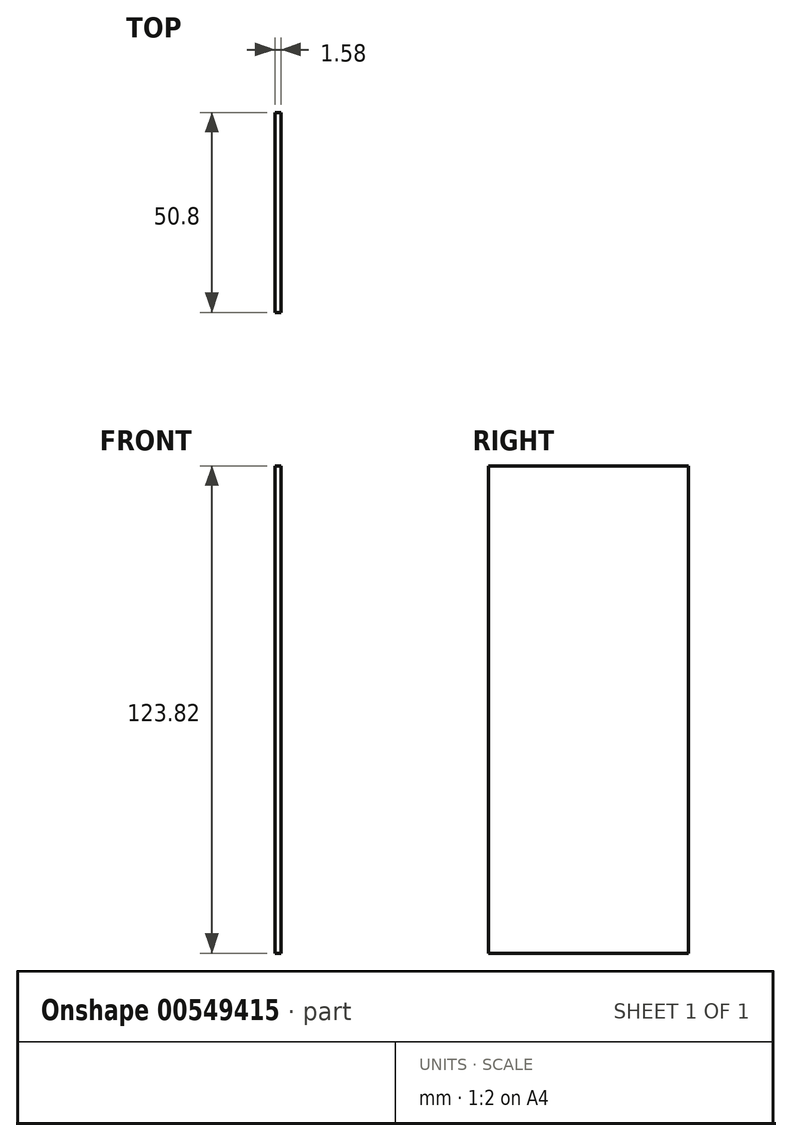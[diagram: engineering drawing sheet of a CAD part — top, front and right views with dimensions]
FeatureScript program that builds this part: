
annotation { "Feature Type Name" : "Feature", "Feature Type Description" : "" }
export const myFeature = defineFeature(function(context is Context, id is Id, definition is map)
    precondition{}
    {
        {
            var Q0;
            Q0=qCreatedBy(makeId("Right.planeOp"),FACE);
            var sketch = newSketch(context, id + "F0", { "sketchPlane" : qUnion([Q0])});
            skLineSegment(sketch, "E0.bottom", {"start": v(-25.4, 61.91) * mm, "end": v(25.4, 61.91) * mm});
            skLineSegment(sketch, "E0.top", {"start": v(-25.4, -61.91) * mm, "end": v(25.4, -61.91) * mm});
            skLineSegment(sketch, "E0.left", {"start": v(-25.4, 61.91) * mm, "end": v(-25.4, -61.91) * mm});
            skLineSegment(sketch, "E0.right", {"start": v(25.4, 61.91) * mm, "end": v(25.4, -61.91) * mm});
            skSolve(sketch);
        }
        {
            var Q0;
            Q0=makeQuery(id+"F0.imprint","IMPRINT",FACE,{"disambiguationData":[TD([[makeQuery(id+"F0.imprint","IMPRINT",EDGE,{"derivedFrom":sQuery(id+"F0.wireOp",EDGE,"E0.bottom")}),-1.0]])]});
            extrude(context, id + "F1", {"entities" : qUnion([Q0]), "endBound" : BoundingType.SYMMETRIC, "depth" : 1.59 * mm, "offsetDistance" : 25.4 * mm});
        }
    });
